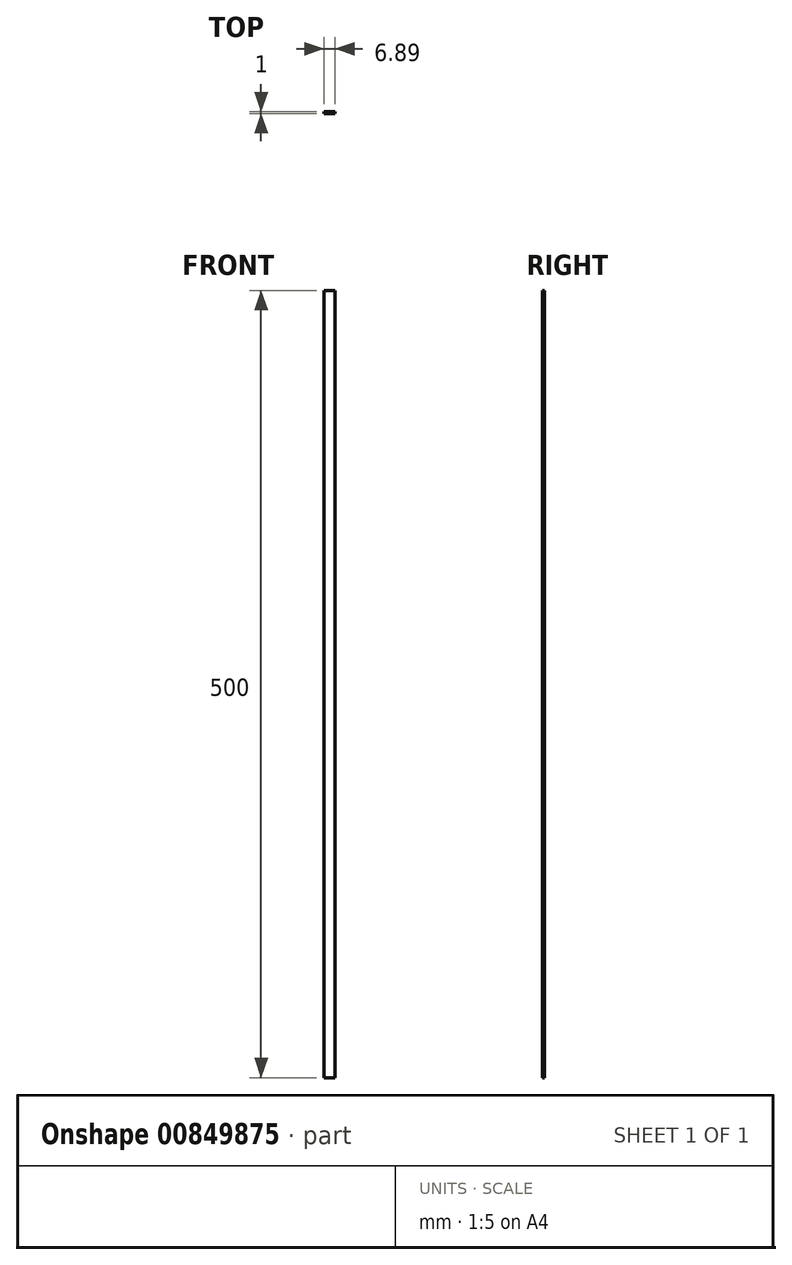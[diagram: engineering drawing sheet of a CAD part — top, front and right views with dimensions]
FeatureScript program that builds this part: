
annotation { "Feature Type Name" : "Feature", "Feature Type Description" : "" }
export const myFeature = defineFeature(function(context is Context, id is Id, definition is map)
    precondition{}
    {
        {
            var Q0;
            Q0=qCreatedBy(makeId("Front.planeOp"),FACE);
            var sketch = newSketch(context, id + "F0", { "sketchPlane" : qUnion([Q0])});
            skLineSegment(sketch, "E0.bottom", {"start": v(-33.67, 247.33) * mm, "end": v(-26.78, 247.33) * mm});
            skLineSegment(sketch, "E0.top", {"start": v(-33.67, -252.67) * mm, "end": v(-26.78, -252.67) * mm});
            skLineSegment(sketch, "E0.left", {"start": v(-33.67, 247.33) * mm, "end": v(-33.67, -252.67) * mm});
            skLineSegment(sketch, "E0.right", {"start": v(-26.78, 247.33) * mm, "end": v(-26.78, -252.67) * mm});
            skSolve(sketch);
        }
        {
            var Q0;
            Q0=makeQuery(id+"F0.imprint","IMPRINT",FACE,{"disambiguationData":[TD([[makeQuery(id+"F0.imprint","IMPRINT",EDGE,{"derivedFrom":sQuery(id+"F0.wireOp",EDGE,"E0.bottom")}),-1.0]])]});
            extrude(context, id + "F1", {"entities" : qUnion([Q0]), "depth" : 1 * mm, "offsetDistance" : 25 * mm});
        }
    });
